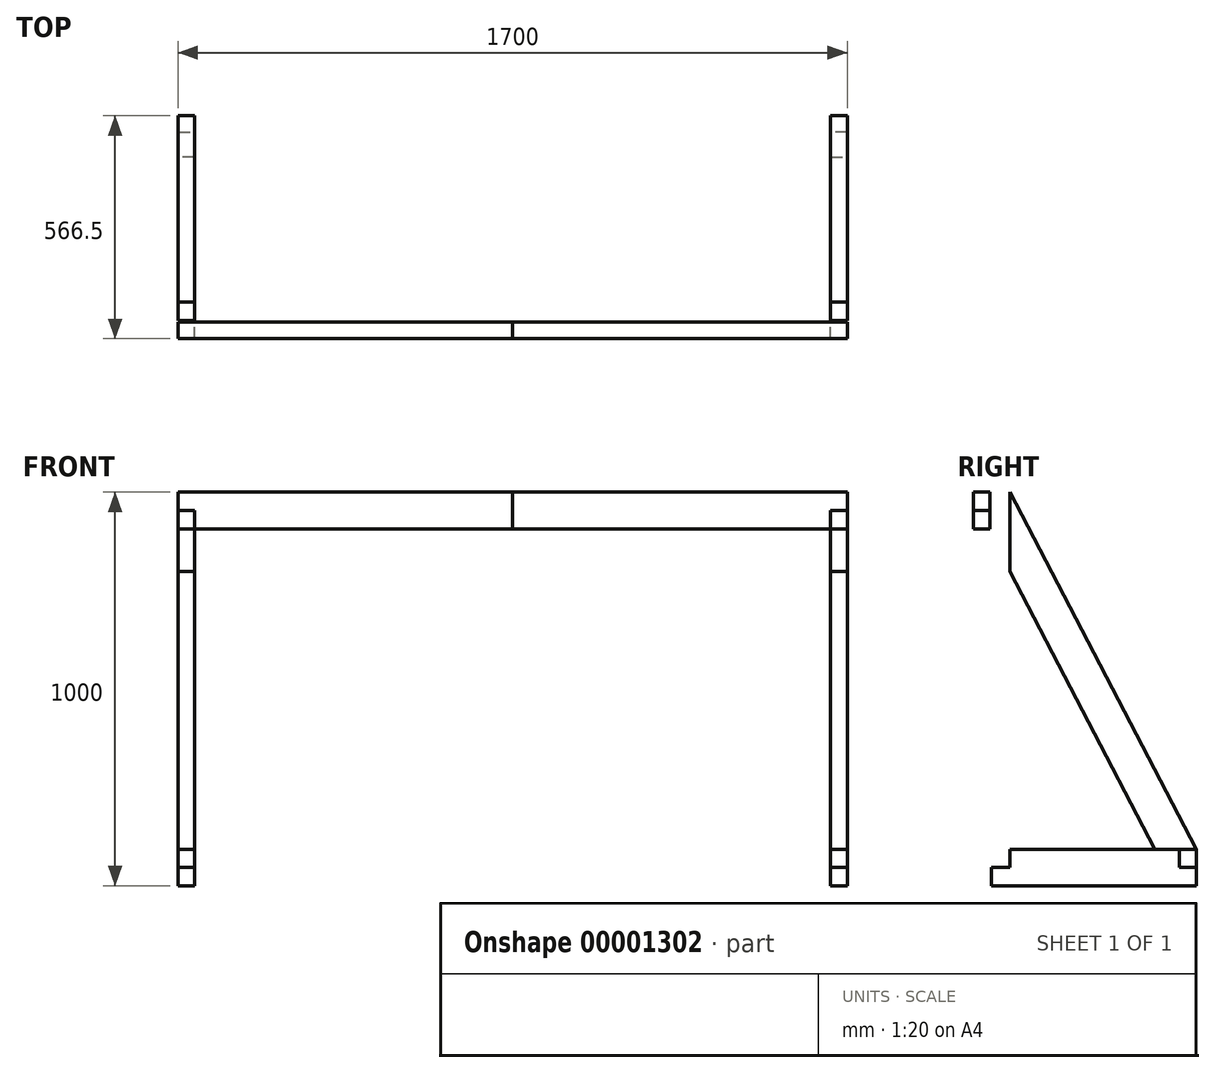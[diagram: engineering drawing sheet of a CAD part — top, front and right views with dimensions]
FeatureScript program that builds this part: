
annotation { "Feature Type Name" : "Feature", "Feature Type Description" : "" }
export const myFeature = defineFeature(function(context is Context, id is Id, definition is map)
    precondition{}
    {
        {
            var Q0;
            Q0=qCreatedBy(makeId("Front.planeOp"),FACE);
            var sketch = newSketch(context, id + "F0", { "sketchPlane" : qUnion([Q0])});
            skLineSegment(sketch, "E0.bottom", {"start": v(0, 1000) * mm, "end": v(-808, 1000) * mm});
            skLineSegment(sketch, "E0.top", {"start": v(0, 1093) * mm, "end": v(-850, 1093) * mm});
            skLineSegment(sketch, "E0.left", {"start": v(0, 1000) * mm, "end": v(0, 1093) * mm});
            skLineSegment(sketch, "E0.right", {"start": v(-850, 1046.5) * mm, "end": v(-850, 1093) * mm});
            skLineSegment(sketch, "E1", {"start": v(-850, 1046.5) * mm, "end": v(-808, 1046.5) * mm});
            skLineSegment(sketch, "E2", {"start": v(-808, 1046.5) * mm, "end": v(-808, 1000) * mm});
            skPoint(sketch, "E3.orphan", {"position": v(-850, 1000) * mm});
            skSolve(sketch);
        }
        {
            var Q0;
            Q0 = qSketchRegion(id + "F0", true);
            extrude(context, id + "F1", {"entities" : qUnion([Q0]), "depth" : 42 * mm});
        }
        {
            var Q0;
            Q0=makeQuery(id+"F1.opExtrude","SWEPT_FACE",FACE,{"disambiguationData":[OSD([sQuery(id+"F0.wireOp",EDGE,"E2")])]});
            var sketch = newSketch(context, id + "F2", { "sketchPlane" : qUnion([Q0])});
            skLineSegment(sketch, "E4.0", {"start": v(0, 1046.5) * mm, "end": v(0, 1093) * mm});
            skLineSegment(sketch, "E5.0", {"start": v(42, 1046.5) * mm, "end": v(0, 1046.5) * mm});
            skLineSegment(sketch, "E6.0", {"start": v(42, 1046.5) * mm, "end": v(42, 1000) * mm});
            skLineSegment(sketch, "E7", {"start": v(0, 1093) * mm, "end": v(0, 1046.5) * mm});
            skLineSegment(sketch, "E8", {"start": v(42, 1046.5) * mm, "end": v(42, 93) * mm});
            skLineSegment(sketch, "E9", {"start": v(42, 93) * mm, "end": v(-4.5, 93) * mm});
            skLineSegment(sketch, "E10", {"start": v(-4.5, 93) * mm, "end": v(-4.5, 139.5) * mm});
            skLineSegment(sketch, "E11", {"start": v(-4.5, 139.5) * mm, "end": v(-51, 139.5) * mm});
            skLineSegment(sketch, "E12", {"start": v(-51, 139.5) * mm, "end": v(-51, 1093) * mm});
            skLineSegment(sketch, "E13", {"start": v(-51, 1093) * mm, "end": v(0, 1093) * mm});
            skSolve(sketch);
        }
        {
            var Q0;
            Q0=makeQuery(id+"F2.imprint","IMPRINT",FACE,{"disambiguationData":[TD([[makeQuery(id+"F2.imprint","IMPRINT",EDGE,{"derivedFrom":sQuery(id+"F2.wireOp",EDGE,"E7")}),-1.0]])]});
            var Q1;
            {var subQ3=sQuery(id+"F2.wireOp",EDGE,"E5.0");Q1=makeQuery(id+"F2.imprint","IMPRINT",FACE,{"disambiguationData":[TD([[makeQuery(id+"F2.imprint","IMPRINT",EDGE,{"derivedFrom":subQ3}),1.0]])]});}
            var Q2;
            Q2=makeQuery(id+"F1.opExtrude","SWEPT_FACE",FACE,{"disambiguationData":[OSD([sQuery(id+"F0.wireOp",EDGE,"E0.right")])]});
            extrude(context, id + "F3", {"entities" : qUnion([Q0, Q1]), "endBound" : BoundingType.UP_TO_SURFACE, "endBoundEntityFace" : qUnion([Q2]), "depth" : 25 * mm});
        }
        {
            var Q0;
            Q0=makeQuery(id+"F3.opExtrude","CAP_FACE",FACE,{"disambiguationData":[OSD([sQuery(id+"F2.wireOp",EDGE,"E5.0"),sQuery(id+"F2.wireOp",EDGE,"E7"),sQuery(id+"F2.wireOp",EDGE,"E8"),sQuery(id+"F2.wireOp",EDGE,"E9"),sQuery(id+"F2.wireOp",EDGE,"E10"),sQuery(id+"F2.wireOp",EDGE,"E11"),sQuery(id+"F2.wireOp",EDGE,"E12"),sQuery(id+"F2.wireOp",EDGE,"E13")])],"isStart":true});
            var sketch = newSketch(context, id + "F4", { "sketchPlane" : qUnion([Q0])});
            skLineSegment(sketch, "E14", {"start": v(51, 139.5) * mm, "end": v(4.5, 139.5) * mm});
            skLineSegment(sketch, "E15", {"start": v(4.5, 139.5) * mm, "end": v(4.5, 93) * mm});
            skLineSegment(sketch, "E16", {"start": v(4.5, 93) * mm, "end": v(524.5, 93) * mm});
            skLineSegment(sketch, "E17", {"start": v(524.5, 93) * mm, "end": v(524.5, 139.5) * mm});
            skLineSegment(sketch, "E18", {"start": v(524.5, 139.5) * mm, "end": v(482.5, 139.5) * mm});
            skLineSegment(sketch, "E19", {"start": v(482.5, 139.5) * mm, "end": v(482.5, 186) * mm});
            skLineSegment(sketch, "E20", {"start": v(482.5, 186) * mm, "end": v(51, 186) * mm});
            skLineSegment(sketch, "E21", {"start": v(51, 186) * mm, "end": v(51, 139.5) * mm});
            skSolve(sketch);
        }
        {
            var Q0;
            Q0 = qSketchRegion(id + "F4", true);
            var Q1;
            Q1=makeQuery(id+"F3.opExtrude","CAP_FACE",FACE,{"disambiguationData":[OSD([sQuery(id+"F2.wireOp",EDGE,"E5.0"),sQuery(id+"F2.wireOp",EDGE,"E7"),sQuery(id+"F2.wireOp",EDGE,"E8"),sQuery(id+"F2.wireOp",EDGE,"E9"),sQuery(id+"F2.wireOp",EDGE,"E10"),sQuery(id+"F2.wireOp",EDGE,"E11"),sQuery(id+"F2.wireOp",EDGE,"E12"),sQuery(id+"F2.wireOp",EDGE,"E13")])],"isStart":false});
            extrude(context, id + "F5", {"entities" : qUnion([Q0]), "endBound" : BoundingType.UP_TO_SURFACE, "oppositeDirection" : true, "endBoundEntityFace" : qUnion([Q1]), "depth" : 25 * mm});
        }
        {
            var Q0;
            Q0=makeQuery(id+"F3.opExtrude","CAP_FACE",FACE,{"disambiguationData":[OSD([sQuery(id+"F2.wireOp",EDGE,"E5.0"),sQuery(id+"F2.wireOp",EDGE,"E7"),sQuery(id+"F2.wireOp",EDGE,"E8"),sQuery(id+"F2.wireOp",EDGE,"E9"),sQuery(id+"F2.wireOp",EDGE,"E10"),sQuery(id+"F2.wireOp",EDGE,"E11"),sQuery(id+"F2.wireOp",EDGE,"E12"),sQuery(id+"F2.wireOp",EDGE,"E13")])],"isStart":false});
            var sketch = newSketch(context, id + "F6", { "sketchPlane" : qUnion([Q0])});
            skLineSegment(sketch, "E22.0", {"start": v(-482.5, 186) * mm, "end": v(-51, 186) * mm});
            skLineSegment(sketch, "E23.0", {"start": v(-524.5, 93) * mm, "end": v(-524.5, 139.5) * mm});
            skLineSegment(sketch, "E24.0", {"start": v(-51, 139.5) * mm, "end": v(-51, 1093) * mm});
            skLineSegment(sketch, "E25.0", {"start": v(-51, 1093) * mm, "end": v(0, 1093) * mm});
            skLineSegment(sketch, "E26", {"start": v(-482.5, 186) * mm, "end": v(-635.91, 186) * mm, "construction": true});
            skLineSegment(sketch, "E27", {"start": v(-524.5, 93) * mm, "end": v(-524.5, 301.2) * mm, "construction": true});
            skLineSegment(sketch, "E28", {"start": v(-51, 1093) * mm, "end": v(-524.5, 186) * mm});
            skLineSegment(sketch, "E29", {"start": v(-419.59, 186) * mm, "end": v(-51, 892.04) * mm});
            skLineSegment(sketch, "E30", {"start": v(-51, 892.04) * mm, "end": v(-51, 1093) * mm});
            skLineSegment(sketch, "E31", {"start": v(-524.5, 186) * mm, "end": v(-419.59, 186) * mm});
            skSolve(sketch);
        }
        {
            var Q0;
            {var subQ1=sQuery(id+"F6.wireOp",EDGE,"E28");Q0=makeQuery(id+"F6.imprint","IMPRINT",FACE,{"disambiguationData":[TD([[makeQuery(id+"F6.imprint","IMPRINT",EDGE,{"derivedFrom":subQ1}),1.0]])]});}
            var Q1;
            Q1=makeQuery(id+"F5.opExtrude","CAP_FACE",FACE,{"disambiguationData":[OSD([sQuery(id+"F4.wireOp",EDGE,"E14"),sQuery(id+"F4.wireOp",EDGE,"E15"),sQuery(id+"F4.wireOp",EDGE,"E16"),sQuery(id+"F4.wireOp",EDGE,"E17"),sQuery(id+"F4.wireOp",EDGE,"E18"),sQuery(id+"F4.wireOp",EDGE,"E19"),sQuery(id+"F4.wireOp",EDGE,"E20"),sQuery(id+"F4.wireOp",EDGE,"E21")])],"isStart":true});
            extrude(context, id + "F7", {"entities" : qUnion([Q0]), "endBound" : BoundingType.UP_TO_SURFACE, "oppositeDirection" : true, "endBoundEntityFace" : qUnion([Q1]), "depth" : 25 * mm});
        }
        {
            var Q0;
            Q0=makeQuery(id+"F5.opExtrude","SWEPT_FACE",FACE,{"disambiguationData":[OSD([sQuery(id+"F4.wireOp",EDGE,"E19")])]});
            var sketch = newSketch(context, id + "F8", { "sketchPlane" : qUnion([Q0])});
            skLineSegment(sketch, "E32", {"start": v(850, 186) * mm, "end": v(850, 139.5) * mm});
            skLineSegment(sketch, "E33", {"start": v(850, 139.5) * mm, "end": v(808, 139.5) * mm});
            skLineSegment(sketch, "E34.0", {"start": v(808, 93) * mm, "end": v(808, 139.5) * mm});
            skLineSegment(sketch, "E35", {"start": v(808, 139.5) * mm, "end": v(808, 93) * mm});
            skLineSegment(sketch, "E36", {"start": v(808, 93) * mm, "end": v(0, 93) * mm});
            skLineSegment(sketch, "E37", {"start": v(0, 93) * mm, "end": v(0, 186) * mm});
            skLineSegment(sketch, "E38", {"start": v(0, 186) * mm, "end": v(850, 186) * mm});
            skSolve(sketch);
        }
        {
            var Q0;
            Q0=makeQuery(id+"F8.imprint","IMPRINT",FACE,{"disambiguationData":[TD([[makeQuery(id+"F8.imprint","IMPRINT",EDGE,{"derivedFrom":sQuery(id+"F8.wireOp",EDGE,"E35")}),-1.0]])]});
            var Q1;
            {var subQ2=sQuery(id+"F8.wireOp",EDGE,"E32");Q1=makeQuery(id+"F8.imprint","IMPRINT",FACE,{"disambiguationData":[TD([[makeQuery(id+"F8.imprint","IMPRINT",EDGE,{"derivedFrom":subQ2}),1.0]])]});}
            var Q2;
            Q2=makeQuery(id+"F5.opExtrude","SWEPT_FACE",FACE,{"disambiguationData":[OSD([sQuery(id+"F4.wireOp",EDGE,"E17")])]});
            extrude(context, id + "F9", {"entities" : qUnion([Q0, Q1]), "endBound" : BoundingType.UP_TO_SURFACE, "endBoundEntityFace" : qUnion([Q2]), "depth" : 25 * mm});
        }
        {
            var Q0;
            Q0=makeQuery(id+"F1.opExtrude","SWEPT_BODY",BODY,{"disambiguationData":[OSD([sQuery(id+"F0.wireOp",EDGE,"E0.bottom"),sQuery(id+"F0.wireOp",EDGE,"E0.top"),sQuery(id+"F0.wireOp",EDGE,"E0.left"),sQuery(id+"F0.wireOp",EDGE,"E0.right"),sQuery(id+"F0.wireOp",EDGE,"E1"),sQuery(id+"F0.wireOp",EDGE,"E2")])]});
            var Q1;
            Q1=makeQuery(id+"F7.opExtrude","SWEPT_BODY",BODY,{"disambiguationData":[OSD([sQuery(id+"F6.wireOp",EDGE,"E28"),sQuery(id+"F6.wireOp",EDGE,"E29"),sQuery(id+"F6.wireOp",EDGE,"E30"),sQuery(id+"F6.wireOp",EDGE,"E31")])]});
            var Q2;
            Q2=makeQuery(id+"F3.opExtrude","SWEPT_BODY",BODY,{"disambiguationData":[OSD([sQuery(id+"F2.wireOp",EDGE,"E5.0"),sQuery(id+"F2.wireOp",EDGE,"E7"),sQuery(id+"F2.wireOp",EDGE,"E8"),sQuery(id+"F2.wireOp",EDGE,"E9"),sQuery(id+"F2.wireOp",EDGE,"E10"),sQuery(id+"F2.wireOp",EDGE,"E11"),sQuery(id+"F2.wireOp",EDGE,"E12"),sQuery(id+"F2.wireOp",EDGE,"E13")])]});
            var Q3;
            Q3=makeQuery(id+"F5.opExtrude","SWEPT_BODY",BODY,{"disambiguationData":[OSD([sQuery(id+"F4.wireOp",EDGE,"E14"),sQuery(id+"F4.wireOp",EDGE,"E15"),sQuery(id+"F4.wireOp",EDGE,"E16"),sQuery(id+"F4.wireOp",EDGE,"E17"),sQuery(id+"F4.wireOp",EDGE,"E18"),sQuery(id+"F4.wireOp",EDGE,"E19"),sQuery(id+"F4.wireOp",EDGE,"E20"),sQuery(id+"F4.wireOp",EDGE,"E21")])]});
            var Q4;
            Q4=makeQuery(id+"F9.opExtrude","SWEPT_BODY",BODY,{"disambiguationData":[OSD([sQuery(id+"F8.wireOp",EDGE,"E32"),sQuery(id+"F8.wireOp",EDGE,"E33"),sQuery(id+"F8.wireOp",EDGE,"E35"),sQuery(id+"F8.wireOp",EDGE,"E36"),sQuery(id+"F8.wireOp",EDGE,"E37"),sQuery(id+"F8.wireOp",EDGE,"E38")])]});
            var Q5;
            Q5=makeQuery(id+"F1.opExtrude","SWEPT_FACE",FACE,{"disambiguationData":[OSD([sQuery(id+"F0.wireOp",EDGE,"E0.left")])]});
            mirror(context, id + "F10", {"entities" : qUnion([Q0, Q1, Q2, Q3, Q4]), "mirrorPlane" : qUnion([Q5])});
        }
    });
